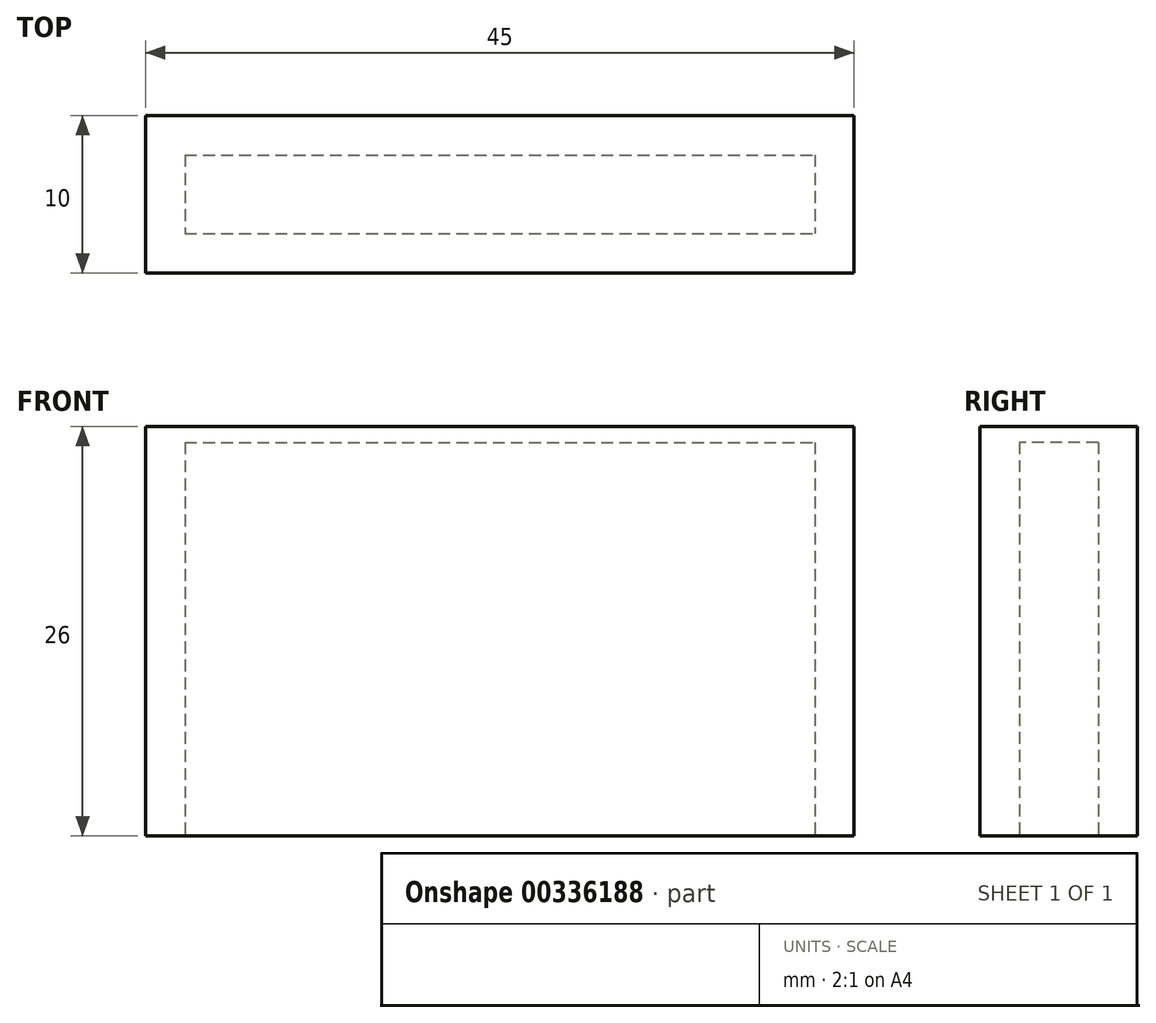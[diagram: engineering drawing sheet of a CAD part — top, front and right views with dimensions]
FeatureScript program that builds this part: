
annotation { "Feature Type Name" : "Feature", "Feature Type Description" : "" }
export const myFeature = defineFeature(function(context is Context, id is Id, definition is map)
    precondition{}
    {
        {
            var Q0;
            Q0=qCreatedBy(makeId("Top.planeOp"),FACE);
            var sketch = newSketch(context, id + "F0", { "sketchPlane" : qUnion([Q0])});
            skLineSegment(sketch, "E0.bottom", {"start": v(-22.5, 5) * mm, "end": v(22.5, 5) * mm});
            skLineSegment(sketch, "E0.top", {"start": v(-22.5, -5) * mm, "end": v(22.5, -5) * mm});
            skLineSegment(sketch, "E0.left", {"start": v(-22.5, 5) * mm, "end": v(-22.5, -5) * mm});
            skLineSegment(sketch, "E0.right", {"start": v(22.5, 5) * mm, "end": v(22.5, -5) * mm});
            skLineSegment(sketch, "E1.bottom", {"start": v(-20, 2.5) * mm, "end": v(20, 2.5) * mm});
            skLineSegment(sketch, "E1.top", {"start": v(-20, -2.5) * mm, "end": v(20, -2.5) * mm});
            skLineSegment(sketch, "E1.left", {"start": v(-20, 2.5) * mm, "end": v(-20, -2.5) * mm});
            skLineSegment(sketch, "E1.right", {"start": v(20, 2.5) * mm, "end": v(20, -2.5) * mm});
            skSolve(sketch);
        }
        {
            var Q0;
            Q0=makeQuery(id+"F0.imprint","IMPRINT",FACE,{"disambiguationData":[TD([[makeQuery(id+"F0.imprint","IMPRINT",EDGE,{"derivedFrom":sQuery(id+"F0.wireOp",EDGE,"E0.bottom")}),-1.0]])]});
            extrude(context, id + "F1", {"entities" : qUnion([Q0]), "depth" : 25 * mm});
        }
        {
            var Q0;
            Q0=makeQuery(id+"F1.opExtrude","CAP_FACE",FACE,{"disambiguationData":[OSD([sQuery(id+"F0.wireOp",EDGE,"E0.bottom"),sQuery(id+"F0.wireOp",EDGE,"E0.top"),sQuery(id+"F0.wireOp",EDGE,"E0.left"),sQuery(id+"F0.wireOp",EDGE,"E0.right"),sQuery(id+"F0.wireOp",EDGE,"E1.bottom"),sQuery(id+"F0.wireOp",EDGE,"E1.top"),sQuery(id+"F0.wireOp",EDGE,"E1.left"),sQuery(id+"F0.wireOp",EDGE,"E1.right")])],"isStart":false});
            var sketch = newSketch(context, id + "F2", { "sketchPlane" : qUnion([Q0])});
            skLineSegment(sketch, "E2.bottom", {"start": v(-22.5, 5) * mm, "end": v(22.5, 5) * mm});
            skLineSegment(sketch, "E2.top", {"start": v(-22.5, -5) * mm, "end": v(22.5, -5) * mm});
            skLineSegment(sketch, "E2.left", {"start": v(-22.5, 5) * mm, "end": v(-22.5, -5) * mm});
            skLineSegment(sketch, "E2.right", {"start": v(22.5, 5) * mm, "end": v(22.5, -5) * mm});
            skSolve(sketch);
        }
        {
            var Q0;
            Q0 = qSketchRegion(id + "F2", true);
            extrude(context, id + "F3", {"entities" : qUnion([Q0]), "operationType" : NewBodyOperationType.ADD, "depth" : 1 * mm});
        }
    });
